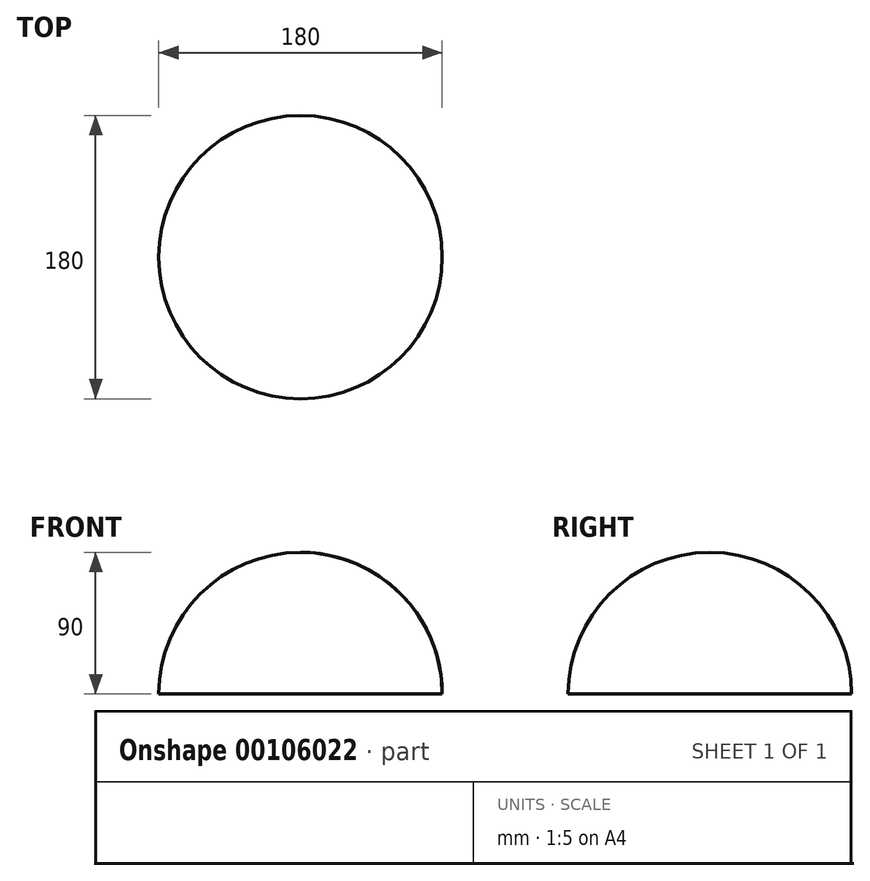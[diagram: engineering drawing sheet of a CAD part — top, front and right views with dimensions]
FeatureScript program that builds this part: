
annotation { "Feature Type Name" : "Feature", "Feature Type Description" : "" }
export const myFeature = defineFeature(function(context is Context, id is Id, definition is map)
    precondition{}
    {
        {
            var Q0;
            Q0=qCreatedBy(makeId("Front.planeOp"),FACE);
            var sketch = newSketch(context, id + "F0", { "sketchPlane" : qUnion([Q0])});
            skArc(sketch, "E0", {"start": v(90, 0) * mm, "mid": v(63.64, 63.64) * mm, "end": v(0, 90) * mm});
            skLineSegment(sketch, "E1", {"start": v(0, 0) * mm, "end": v(0, 90) * mm});
            skLineSegment(sketch, "E2", {"start": v(90, 0) * mm, "end": v(0, 0) * mm});
            skSolve(sketch);
        }
        {
            var Q0;
            Q0=qSketchRegion(id+"F0",true);
            var Q1;
            Q1=sQuery(id+"F0.wireOp",EDGE,"E1");
            revolve(context, id + "F1", {"entities" : qUnion([Q0]), "axis" : qUnion([Q1]), "revolveType" : RevolveType.FULL});
        }
        {
            var Q0;
            Q0=qSketchRegion(id+"F0",true);
            var Q1;
            Q1=sQuery(id+"F0.wireOp",EDGE,"E0");
            var Q2;
            Q2=sQuery(id+"F0.wireOp",EDGE,"E1");
            revolve(context, id + "F2", {"bodyType" : ToolBodyType.SURFACE, "entities" : qUnion([Q0]), "surfaceEntities" : qUnion([Q1]), "axis" : qUnion([Q2]), "revolveType" : RevolveType.FULL});
        }
    });
